# Revit family: svetilnik_alfresco_star mini
name_source: partatom
category: Lighting Fixtures
revit_build: Autodesk Revit 2016 (Build: 20150506_1715(x64)
units: mm (PartAtom-declared; Revit-internal decimal feet)

## family parameters
Always vertical = Yes
Cut with Voids When Loaded = No
Light Source = Yes
Part Type = Normal
Room Calculation Point = No
Round Connector Dimension = Use Diameter
Shared = No
Work Plane-Based = No

## types (1)
- STAR мини
    ADSK_Артикул = ДТУ471
    ADSK_Единица измерения = шт.
    ADSK_Завод-изготовитель = ALFRESCO
    ADSK_Количество фаз = 2
    ADSK_Количество фаз числовое = 2
    ADSK_Коэффициент мощности = 0.98
    ADSK_Масса = 2
    ADSK_Модель = ДТУ-47-AF STAR мини
    ADSK_Наименование = Светодиодный светильник STAR мини ДТУ-47-AF-7Вт-0,65
    ADSK_Напряжение = 220 V
    ADSK_Номинальная мощность = 7 W
    ADSK_Полная мощность = 7 VA
    ADSK_Размер_Высота = 650 mm  [stored 2.13255 ft]
    ADSK_Размер_Диаметр = 90 mm  [stored 0.295276 ft]
    ADSK_Ток = 0 A
    ADSK_Энергоэффективность = 100 lm/W
    Apparent Load = 7 VA
    Color Filter = 16777215
    Dimming Lamp Color Temperature Shift = <None>
    Emit Shape Visible in Rendering = No
    Emit from Circle Diameter = 80 mm  [stored 0.262467 ft]
    IP Class = IP 65
    Manufacturer = ALFRESCO
    Photometric Web File = ДТУ-47-AF Star mini 7W.ies
    Tilt Angle = 90.00°
    URL = http://www.allfresco.ru
    Блок аварийного питания = No
    Класс защиты = 1
    Класс пожароопасности = F (светильники предназначены для установки непосредственно на поверхность из нормально воспламеняемых материалов)
    Климатическая зона = У1
    Корпус светильника = Сталь крашенная чёрная
    Материал рассеивателя = Прозрачное закаленное стекло
    Область использования = ландшафт, коттедж. Посёлки,микрорайоны
    Плафон = Прозрачное закаленное стекло
    Температура эксплуатации = -35 +40
    Тип ИС = LED-светодиоды
    Тип КСС = Круглосимметричная
    Тип ПРА = -
    Тип продукции = LED-светильник
    Цветовая температура = 2700-6500

note: [stored X ft] marks values corroborated as IEEE doubles in the binary element streams (Revit-internal decimal feet)

## geometry (parser evidence)
native form markers: Blend x2
no freeform markers — native parametric forms only
